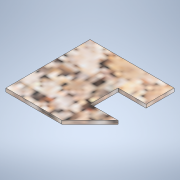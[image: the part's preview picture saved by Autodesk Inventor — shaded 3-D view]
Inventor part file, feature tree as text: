
AUTODESK INVENTOR PART (.ipt)
format: ipt  version: 2020 (Build 240168000, 168)  size: 121,856 bytes
history: native  units: in
note: dims shown in document units (in); Inventor stores cm internally (conversion verified against a paired STEP export)
features: extrude x1, sketch x1
ambient origin geometry x8: Origin, YZ Plane, XZ Plane, XY Plane, X Axis, Y Axis, Z Axis, Center Point
bodies: Solid1 (feature_tree)
feature tree (2):
  extrude  "Extrusion1"  Depth=1.0in
  sketch  "Sketch1"  dims[d0=1.0in d1=1.0in d4=0.5in d5=0.5in d6=0.063in d7=0.0in]
